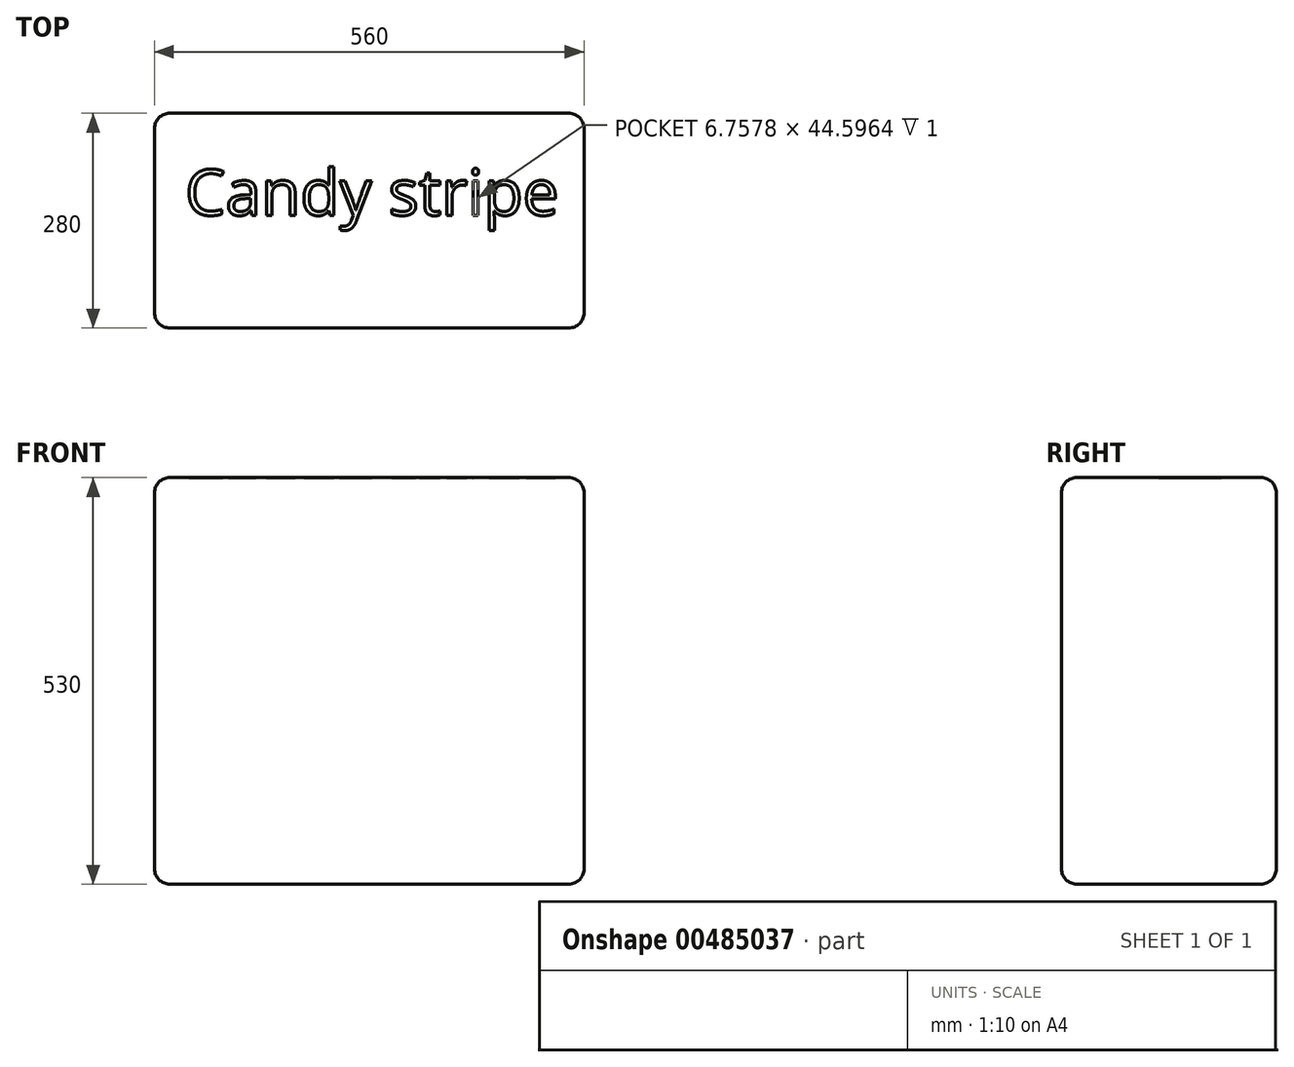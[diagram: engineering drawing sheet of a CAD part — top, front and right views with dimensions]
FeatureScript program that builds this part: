
annotation { "Feature Type Name" : "Feature", "Feature Type Description" : "" }
export const myFeature = defineFeature(function(context is Context, id is Id, definition is map)
    precondition{}
    {
        {
            var Q0;
            Q0=qCreatedBy(makeId("Top.planeOp"),FACE);
            var sketch = newSketch(context, id + "F0", { "sketchPlane" : qUnion([Q0])});
            skLineSegment(sketch, "E0.bottom", {"start": v(280, -140) * mm, "end": v(-280, -140) * mm});
            skLineSegment(sketch, "E0.top", {"start": v(280, 140) * mm, "end": v(-280, 140) * mm});
            skLineSegment(sketch, "E0.left", {"start": v(280, -140) * mm, "end": v(280, 140) * mm});
            skLineSegment(sketch, "E0.right", {"start": v(-280, -140) * mm, "end": v(-280, 140) * mm});
            skPoint(sketch, "E0.middle", {"position": v(0, 0) * mm});
            skSolve(sketch);
        }
        {
            var Q0;
            Q0=qSketchRegion(id+"F0",true);
            extrude(context, id + "F1", {"entities" : qUnion([Q0]), "depth" : 530 * mm, "offsetDistance" : 25 * mm});
        }
        {
            var Q0;
            Q0=makeQuery(id+"F1.opExtrude","CAP_FACE",FACE,{"disambiguationData":[OSD([sQuery(id+"F0.wireOp",EDGE,"E0.bottom"),sQuery(id+"F0.wireOp",EDGE,"E0.top"),sQuery(id+"F0.wireOp",EDGE,"E0.left"),sQuery(id+"F0.wireOp",EDGE,"E0.right")])],"isStart":false});
            var Q1;
            Q1=makeQuery(id+"F1.opExtrude","SWEPT_EDGE",EDGE,{"disambiguationData":[OSD([sQuery(id+"F0.wireOp",EDGE,"E0.top"),sQuery(id+"F0.wireOp",EDGE,"E0.left")])]});
            var Q2;
            Q2=makeQuery(id+"F1.opExtrude","CAP_FACE",FACE,{"disambiguationData":[OSD([sQuery(id+"F0.wireOp",EDGE,"E0.bottom"),sQuery(id+"F0.wireOp",EDGE,"E0.top"),sQuery(id+"F0.wireOp",EDGE,"E0.left"),sQuery(id+"F0.wireOp",EDGE,"E0.right")])],"isStart":true});
            var Q3;
            Q3=makeQuery(id+"F1.opExtrude","SWEPT_EDGE",EDGE,{"disambiguationData":[OSD([sQuery(id+"F0.wireOp",EDGE,"E0.bottom"),sQuery(id+"F0.wireOp",EDGE,"E0.right")])]});
            var Q4;
            Q4=makeQuery(id+"F1.opExtrude","SWEPT_FACE",FACE,{"disambiguationData":[OSD([sQuery(id+"F0.wireOp",EDGE,"E0.bottom")])]});
            var Q5;
            Q5=makeQuery(id+"F1.opExtrude","SWEPT_EDGE",EDGE,{"disambiguationData":[OSD([sQuery(id+"F0.wireOp",EDGE,"E0.bottom"),sQuery(id+"F0.wireOp",EDGE,"E0.left")])]});
            var Q6;
            Q6=makeQuery(id+"F1.opExtrude","CAP_EDGE",EDGE,{"disambiguationData":[OSD([sQuery(id+"F0.wireOp",EDGE,"E0.bottom")])],"isStart":true});
            var Q7;
            Q7=makeQuery(id+"F1.opExtrude","SWEPT_FACE",FACE,{"disambiguationData":[OSD([sQuery(id+"F0.wireOp",EDGE,"E0.left")])]});
            var Q8;
            Q8=makeQuery(id+"F1.opExtrude","CAP_EDGE",EDGE,{"disambiguationData":[OSD([sQuery(id+"F0.wireOp",EDGE,"E0.bottom")])],"isStart":false});
            var Q9;
            Q9=makeQuery(id+"F1.opExtrude","CAP_EDGE",EDGE,{"disambiguationData":[OSD([sQuery(id+"F0.wireOp",EDGE,"E0.top")])],"isStart":false});
            var Q10;
            Q10=makeQuery(id+"F1.opExtrude","CAP_EDGE",EDGE,{"disambiguationData":[OSD([sQuery(id+"F0.wireOp",EDGE,"E0.left")])],"isStart":true});
            var Q11;
            Q11=makeQuery(id+"F1.opExtrude","CAP_EDGE",EDGE,{"disambiguationData":[OSD([sQuery(id+"F0.wireOp",EDGE,"E0.left")])],"isStart":false});
            var Q12;
            Q12=makeQuery(id+"F1.opExtrude","CAP_EDGE",EDGE,{"disambiguationData":[OSD([sQuery(id+"F0.wireOp",EDGE,"E0.right")])],"isStart":false});
            var Q13;
            Q13=makeQuery(id+"F1.opExtrude","SWEPT_EDGE",EDGE,{"disambiguationData":[OSD([sQuery(id+"F0.wireOp",EDGE,"E0.top"),sQuery(id+"F0.wireOp",EDGE,"E0.right")])]});
            var Q14;
            Q14=makeQuery(id+"F1.opExtrude","SWEPT_FACE",FACE,{"disambiguationData":[OSD([sQuery(id+"F0.wireOp",EDGE,"E0.right")])]});
            var Q15;
            Q15=makeQuery(id+"F1.opExtrude","CAP_EDGE",EDGE,{"disambiguationData":[OSD([sQuery(id+"F0.wireOp",EDGE,"E0.top")])],"isStart":true});
            var Q16;
            Q16=makeQuery(id+"F1.opExtrude","CAP_EDGE",EDGE,{"disambiguationData":[OSD([sQuery(id+"F0.wireOp",EDGE,"E0.right")])],"isStart":true});
            var Q17;
            Q17=makeQuery(id+"F1.opExtrude","SWEPT_FACE",FACE,{"disambiguationData":[OSD([sQuery(id+"F0.wireOp",EDGE,"E0.top")])]});
            fillet(context, id + "F2", {"entities" : qUnion([Q0, Q1, Q2, Q3, Q4, Q5, Q6, Q7, Q8, Q9, Q10, Q11, Q12, Q13, Q14, Q15, Q16, Q17]), "radius" : 20 * mm, "tangentPropagation" : true, "allowEdgeOverflow" : false});
        }
        {
            var Q0;
            Q0=makeQuery(id+"F1.opExtrude","CAP_FACE",FACE,{"disambiguationData":[OSD([sQuery(id+"F0.wireOp",EDGE,"E0.bottom"),sQuery(id+"F0.wireOp",EDGE,"E0.top"),sQuery(id+"F0.wireOp",EDGE,"E0.left"),sQuery(id+"F0.wireOp",EDGE,"E0.right")])],"isStart":false});
            var sketch = newSketch(context, id + "F3", { "sketchPlane" : qUnion([Q0])});
            skText(sketch, "E1", { "text": "Candy stripe", "fontName": "OpenSans-Regular.ttf"});
            const initialGuessF3  = {"E1": [-0.24, 0.00704, 1, 0, 0.06]};
            skSetInitialGuess(sketch, initialGuessF3);
            skSolve(sketch);
        }
        {
            var Q0;
            Q0=qSketchRegion(id+"F3",true);
            extrude(context, id + "F4", {"entities" : qUnion([Q0]), "operationType" : NewBodyOperationType.REMOVE, "oppositeDirection" : true, "depth" : 1 * mm});
        }
    });
